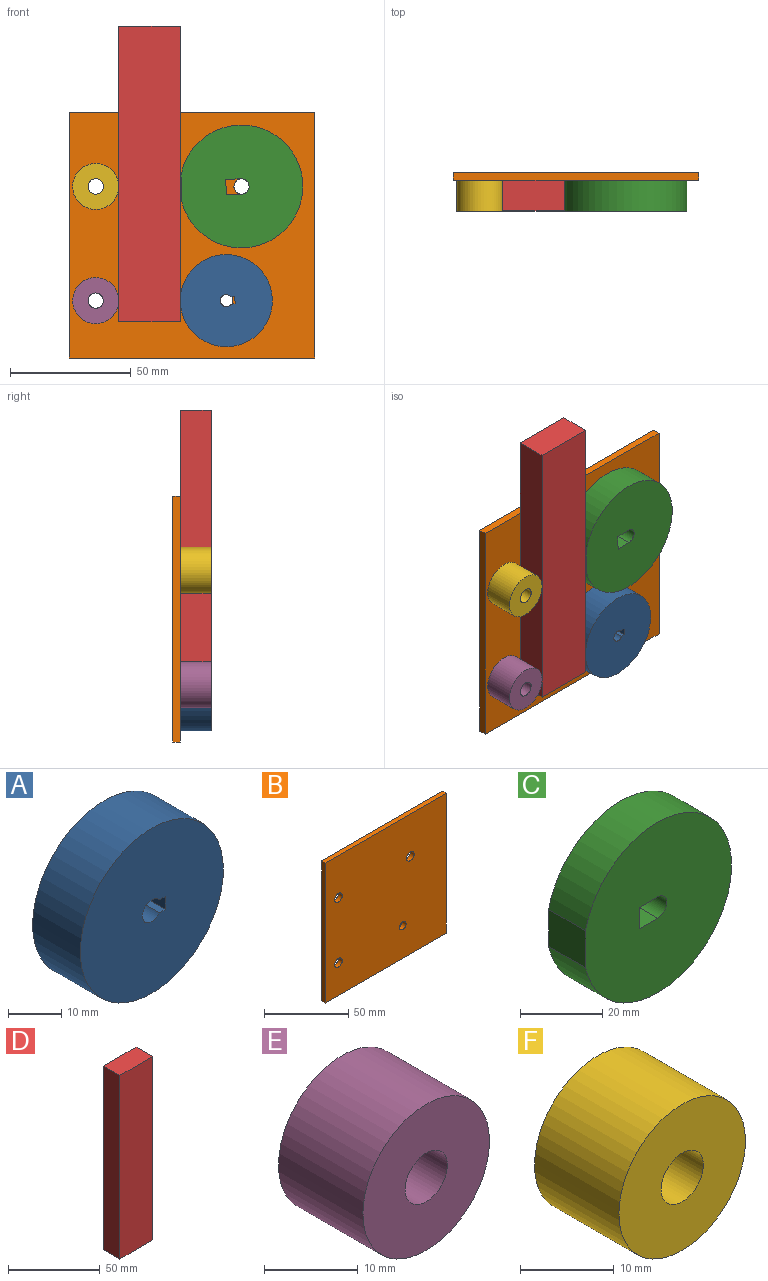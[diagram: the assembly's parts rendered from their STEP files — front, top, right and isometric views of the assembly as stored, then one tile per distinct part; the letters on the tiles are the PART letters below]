
ASSEMBLY  parts=6 mates=6
PART A: 7 faces, bbox 38.1x12.7x38.1 mm
  f0: cylinder r=19.05mm len=38.1mm, axis (0,1,0), area 1520.1mm2, adj f1,f2
  f1: plane 38.1x38.1mm, normal (0,-1,0), area 1116.7mm2, adj f0,f3,f4,f5,f6
  f2: plane 38.1x38.1mm, normal (0,1,0), area 1116.7mm2, adj f0,f3,f4,f5,f6
  f3: cylinder r=2.5mm len=12.7mm, axis (0,-1,0), area 158.7mm2, adj f1,f2,f4,f6
  f4: plane 12.7x1.59mm, normal (0,0,1), area 20.2mm2, adj f1,f2,f3,f5
  f5: plane 12.7x3mm, normal (-1,0,0), area 38.1mm2, adj f1,f2,f4,f6
  f6: plane 12.7x1.59mm, normal (0,0,-1), area 20.2mm2, adj f1,f2,f3,f5
PART B: 10 faces, bbox 101.6x3.2x101.6 mm
  f0: plane 101.6x3.18mm, normal (0,0,1), area 322.6mm2, adj f1,f4,f5,f6
  f1: plane 101.6x3.18mm, normal (-1,0,0), area 322.6mm2, adj f0,f2,f5,f6
  f2: plane 101.6x3.18mm, normal (0,0,-1), area 322.6mm2, adj f1,f4,f5,f6
  f3: cylinder r=2.75mm len=5.51mm, axis (0,-1,0), area 54.9mm2, adj f5,f6
  f4: plane 101.6x3.18mm, normal (1,0,0), area 322.6mm2, adj f0,f2,f5,f6
  f5: plane 101.6x101.6mm, normal (0,1,0), area 10203.7mm2, adj f0,f1,f2,f3,f4,f7,f8,f9
  f6: plane 101.6x101.6mm, normal (0,-1,0), area 10203.7mm2, adj f0,f1,f2,f3,f4,f7,f8,f9
  f7: cylinder r=3.17mm len=6.35mm, axis (0,-1,0), area 63.3mm2, adj f5,f6
  f8: cylinder r=3.17mm len=6.35mm, axis (0,-1,0), area 63.3mm2, adj f5,f6
  f9: cylinder r=3.17mm len=6.35mm, axis (0,-1,0), area 63.3mm2, adj f5,f6
PART C: 8 faces, bbox 50.2x12.7x50.8 mm
  f0: cylinder r=25.4mm len=50.8mm, axis (0,1,0), area 1886.1mm2, adj f5,f6,f7
  f1: cylinder r=3.17mm len=12.7mm, axis (0,1,0), area 126.7mm2, adj f2,f4,f6,f7
  f2: plane 12.7x6.35mm, normal (0,0,1), area 80.6mm2, adj f1,f3,f6,f7
  f3: plane 12.7x6.35mm, normal (1,0,0), area 80.6mm2, adj f2,f4,f6,f7
  f4: plane 12.7x6.35mm, normal (0,0,-1), area 80.6mm2, adj f1,f3,f6,f7
  f5: plane 12.7x11mm, normal (-1,0,0), area 139.6mm2, adj f0,f6,f7
  f6: plane 50.8x50.2mm, normal (0,-1,0), area 1966.2mm2, adj f0,f1,f2,f3,f4,f5
  f7: plane 50.8x50.2mm, normal (0,1,0), area 1966.2mm2, adj f0,f1,f2,f3,f4,f5
PART D: 6 faces, bbox 25.4x12.7x122.3 mm
  f0: plane 122.34x12.7mm, normal (-1,0,0), area 1553.7mm2, adj f1,f3,f4,f5
  f1: plane 25.4x12.7mm, normal (0,0,-1), area 322.6mm2, adj f0,f2,f4,f5
  f2: plane 122.34x12.7mm, normal (1,0,0), area 1553.7mm2, adj f1,f3,f4,f5
  f3: plane 25.4x12.7mm, normal (0,0,1), area 322.6mm2, adj f0,f2,f4,f5
  f4: plane 122.34x25.4mm, normal (0,-1,0), area 3107.3mm2, adj f0,f1,f2,f3
  f5: plane 122.34x25.4mm, normal (0,1,0), area 3107.3mm2, adj f0,f1,f2,f3
PART E: 4 faces, bbox 19.1x12.7x19.1 mm
  f0: cylinder r=3.17mm len=12.7mm, axis (0,1,0), area 253.4mm2, adj f2,f3
  f1: cylinder r=9.53mm len=19.05mm, axis (0,1,0), area 760.1mm2, adj f2,f3
  f2: plane 19.05x19.05mm, normal (0,-1,0), area 253.4mm2, adj f0,f1
  f3: plane 19.05x19.05mm, normal (0,1,0), area 253.4mm2, adj f0,f1
PART F: 4 faces, bbox 19.1x12.7x19.1 mm
  f0: cylinder r=3.17mm len=12.7mm, axis (0,1,0), area 253.4mm2, adj f2,f3
  f1: cylinder r=9.53mm len=19.05mm, axis (0,1,0), area 760.1mm2, adj f2,f3
  f2: plane 19.05x19.05mm, normal (0,-1,0), area 253.4mm2, adj f0,f1
  f3: plane 19.05x19.05mm, normal (0,1,0), area 253.4mm2, adj f0,f1
PLACE A rot(axis=(0,-1,0),2.1deg) t=(11.17,59.88,-39.61)mm
PLACE B t=(11.17,59.88,-39.61)mm fixed
PLACE C rot(axis=(0,-1,0),2.1deg) t=(12.76,59.88,-39.81)mm
PLACE D t=(11.17,59.88,-3.96)mm
PLACE E rot(axis=(0,-1,0),179.5deg) t=(-96.77,59.88,-39.14)mm
PLACE F rot(axis=(0,-1,0),0.1deg) t=(11.22,59.88,-39.56)mm
MATE revolute F.f0 <-> B.f8  axis (0,1,0) through (-42.8,59.88,7.59)mm
MATE revolute B.f9 <-> E.f0  axis (0,-1,0) through (-42.8,59.88,-39.61)mm
MATE planar D.f5 <-> B.f6  axis (0,1,0) through (-20.58,59.88,12.76)mm
MATE parallel D.f5 <-> B.f6  axis (0,1,0) through (-20.58,59.88,12.76)mm
MATE revolute B.f7 <-> C.f7  axis (0,-1,0) through (17.52,59.88,7.59)mm
MATE revolute A.f3 <-> B.f3  axis (0,1,0) through (11.17,59.88,-39.61)mm
